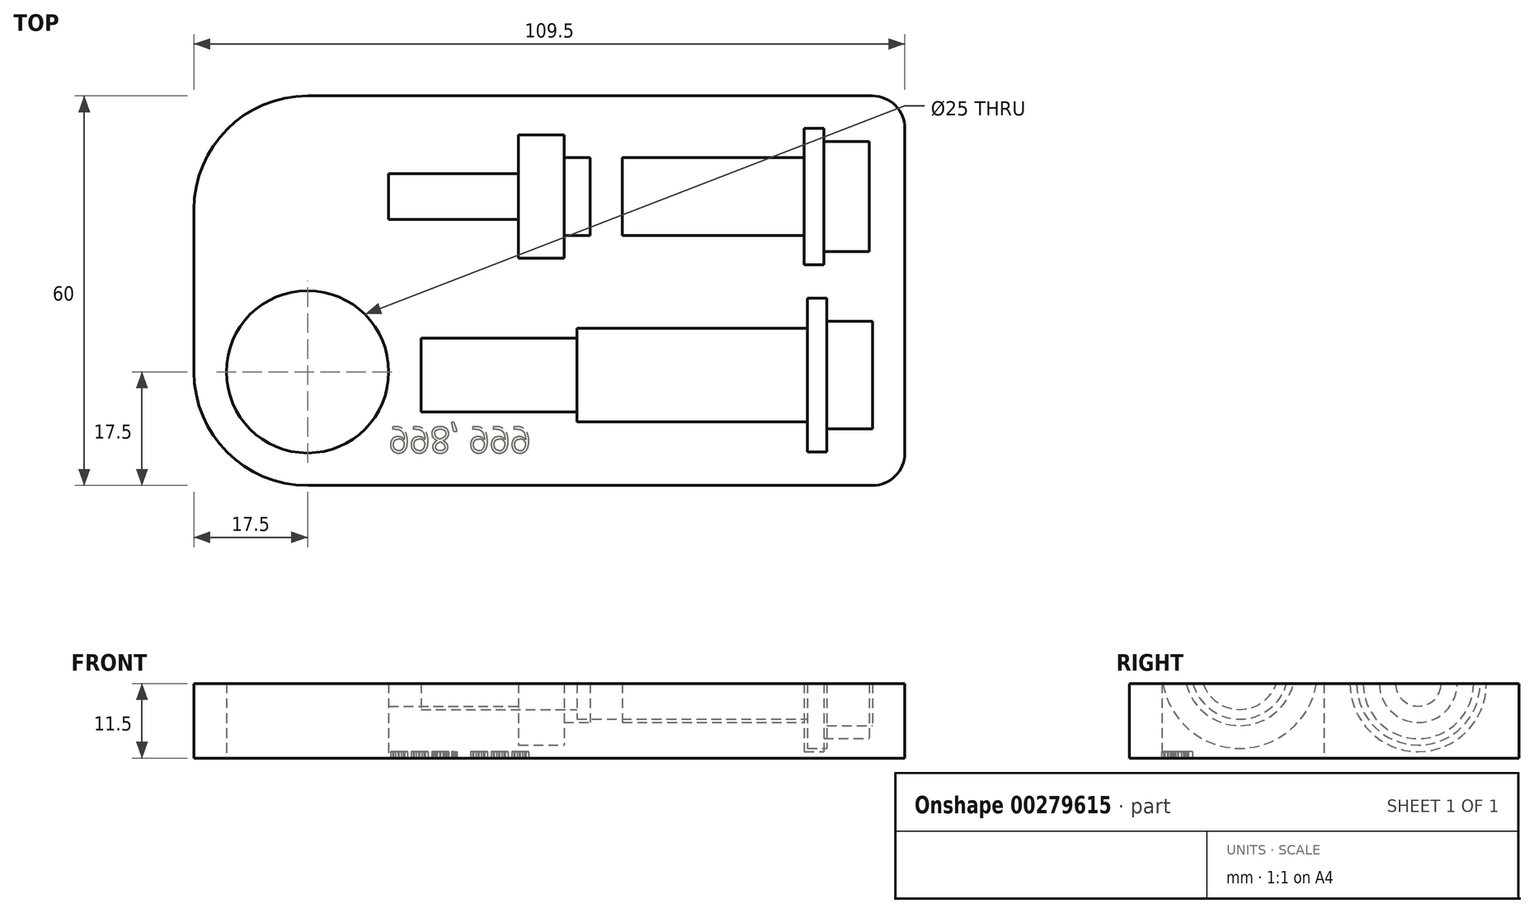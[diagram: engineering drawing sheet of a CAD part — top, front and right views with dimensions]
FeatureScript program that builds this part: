
annotation { "Feature Type Name" : "Feature", "Feature Type Description" : "" }
export const myFeature = defineFeature(function(context is Context, id is Id, definition is map)
    precondition{}
    {
        {
            var Q0;
            Q0=qCreatedBy(makeId("Top.planeOp"),FACE);
            var sketch = newSketch(context, id + "F0", { "sketchPlane" : qUnion([Q0])});
            skLineSegment(sketch, "E0.bottom", {"start": v(17.5, 0) * mm, "end": v(104.5, 0) * mm});
            skLineSegment(sketch, "E0.top", {"start": v(17.5, 60) * mm, "end": v(104.5, 60) * mm});
            skLineSegment(sketch, "E0.left", {"start": v(0, 17.5) * mm, "end": v(0, 42.5) * mm});
            skLineSegment(sketch, "E0.right", {"start": v(109.5, 5) * mm, "end": v(109.5, 55) * mm});
            skLineSegment(sketch, "E1.bottom", {"start": v(0, 0) * mm, "end": v(17.5, 0) * mm, "construction": true});
            skLineSegment(sketch, "E1.top", {"start": v(0, 17.5) * mm, "end": v(17.5, 17.5) * mm, "construction": true});
            skLineSegment(sketch, "E1.left", {"start": v(0, 0) * mm, "end": v(0, 17.5) * mm, "construction": true});
            skLineSegment(sketch, "E1.right", {"start": v(17.5, 0) * mm, "end": v(17.5, 17.5) * mm, "construction": true});
            skCircle(sketch, "E2", {"center": v(17.5, 17.5) * mm, "radius": 12.5 * mm});
            skPoint(sketch, "E3.visualSharp", {"position": v(0, 0) * mm});
            skArc(sketch, "E3.filletArc", {"start": v(0, 17.5) * mm, "mid": v(5.13, 5.13) * mm, "end": v(17.5, 0) * mm});
            skPoint(sketch, "E4.visualSharp", {"position": v(0, 60) * mm});
            skArc(sketch, "E4.filletArc", {"start": v(17.5, 60) * mm, "mid": v(5.13, 54.87) * mm, "end": v(0, 42.5) * mm});
            skPoint(sketch, "E5.visualSharp", {"position": v(109.5, 60) * mm});
            skArc(sketch, "E5.filletArc", {"start": v(109.5, 55) * mm, "mid": v(108.04, 58.54) * mm, "end": v(104.5, 60) * mm});
            skPoint(sketch, "E6.visualSharp", {"position": v(109.5, 0) * mm});
            skArc(sketch, "E6.filletArc", {"start": v(104.5, 0) * mm, "mid": v(108.04, 1.46) * mm, "end": v(109.5, 5) * mm});
            skSolve(sketch);
        }
        {
            var Q0;
            Q0=makeQuery(id+"F0.imprint","IMPRINT",FACE,{"disambiguationData":[TD([[makeQuery(id+"F0.imprint","IMPRINT",EDGE,{"derivedFrom":sQuery(id+"F0.wireOp",EDGE,"E0.bottom")}),1.0]])]});
            extrude(context, id + "F1", {"entities" : qUnion([Q0]), "depth" : 11.5 * mm});
        }
        {
            var Q0;
            Q0=makeQuery(id+"F1.opExtrude","CAP_FACE",FACE,{"disambiguationData":[OSD([sQuery(id+"F0.wireOp",EDGE,"E0.bottom"),sQuery(id+"F0.wireOp",EDGE,"E0.top"),sQuery(id+"F0.wireOp",EDGE,"E0.right"),sQuery(id+"F0.wireOp",EDGE,"E2"),sQuery(id+"F0.wireOp",EDGE,"E3.filletArc"),sQuery(id+"F0.wireOp",EDGE,"E4.filletArc"),sQuery(id+"F0.wireOp",EDGE,"E5.filletArc"),sQuery(id+"F0.wireOp",EDGE,"E6.filletArc")])],"isStart":false});
            var sketch = newSketch(context, id + "F2", { "sketchPlane" : qUnion([Q0])});
            skLineSegment(sketch, "E7.bottom", {"start": v(0, 0) * mm, "end": v(35, 0) * mm, "construction": true});
            skLineSegment(sketch, "E7.top", {"start": v(0, 17) * mm, "end": v(35, 17) * mm, "construction": true});
            skLineSegment(sketch, "E7.left", {"start": v(0, 0) * mm, "end": v(0, 17) * mm, "construction": true});
            skLineSegment(sketch, "E7.right", {"start": v(35, 0) * mm, "end": v(35, 11) * mm, "construction": true});
            skLineSegment(sketch, "E8", {"start": v(35, 17) * mm, "end": v(35, 44.5) * mm, "construction": true});
            skLineSegment(sketch, "E9.bottom", {"start": v(30, 44.5) * mm, "end": v(50, 44.5) * mm});
            skLineSegment(sketch, "E10.bottom", {"start": v(50, 44.5) * mm, "end": v(57, 44.5) * mm});
            skLineSegment(sketch, "E10.top", {"start": v(50, 35) * mm, "end": v(57, 35) * mm});
            skLineSegment(sketch, "E10.left", {"start": v(50, 41) * mm, "end": v(50, 35) * mm});
            skLineSegment(sketch, "E10.right", {"start": v(57, 38.5) * mm, "end": v(57, 35) * mm});
            skLineSegment(sketch, "E11.bottom", {"start": v(57, 44.5) * mm, "end": v(61, 44.5) * mm});
            skLineSegment(sketch, "E11.top", {"start": v(57, 38.5) * mm, "end": v(61, 38.5) * mm});
            skLineSegment(sketch, "E11.right", {"start": v(61, 44.5) * mm, "end": v(61, 38.5) * mm});
            skLineSegment(sketch, "E12", {"start": v(61, 44.5) * mm, "end": v(66, 44.5) * mm, "construction": true});
            skLineSegment(sketch, "E13.bottom", {"start": v(66, 44.5) * mm, "end": v(94, 44.5) * mm});
            skLineSegment(sketch, "E13.top", {"start": v(66, 38.5) * mm, "end": v(94, 38.5) * mm});
            skLineSegment(sketch, "E13.left", {"start": v(66, 44.5) * mm, "end": v(66, 38.5) * mm});
            skLineSegment(sketch, "E14.bottom", {"start": v(94, 44.5) * mm, "end": v(97, 44.5) * mm});
            skLineSegment(sketch, "E14.top", {"start": v(94, 34) * mm, "end": v(97, 34) * mm});
            skLineSegment(sketch, "E14.left", {"start": v(94, 38.5) * mm, "end": v(94, 34) * mm});
            skLineSegment(sketch, "E14.right", {"start": v(97, 36) * mm, "end": v(97, 34) * mm});
            skLineSegment(sketch, "E15.bottom", {"start": v(97, 44.5) * mm, "end": v(104, 44.5) * mm});
            skLineSegment(sketch, "E15.top", {"start": v(97, 36) * mm, "end": v(104, 36) * mm});
            skLineSegment(sketch, "E15.right", {"start": v(104, 44.5) * mm, "end": v(104, 36) * mm});
            skLineSegment(sketch, "E16", {"start": v(35, 44.5) * mm, "end": v(30, 44.5) * mm, "construction": true});
            skLineSegment(sketch, "E17", {"start": v(50, 41) * mm, "end": v(30, 41) * mm});
            skLineSegment(sketch, "E18", {"start": v(30, 41) * mm, "end": v(30, 44.5) * mm});
            skSolve(sketch);
        }
        {
            var Q0;
            Q0=makeQuery(id+"F2.imprint","IMPRINT",FACE,{"disambiguationData":[TD([[makeQuery(id+"F2.imprint","IMPRINT",EDGE,{"derivedFrom":sQuery(id+"F2.wireOp",EDGE,"E9.bottom")}),-1.0]])]});
            var Q1;
            Q1=makeQuery(id+"F2.imprint","IMPRINT",FACE,{"disambiguationData":[TD([[makeQuery(id+"F2.imprint","IMPRINT",EDGE,{"derivedFrom":sQuery(id+"F2.wireOp",EDGE,"E13.bottom")}),-1.0]])]});
            var Q2;
            Q2=sQuery(id+"F2.wireOp",EDGE,"E13.bottom");
            revolve(context, id + "F3", {"operationType" : NewBodyOperationType.REMOVE, "entities" : qUnion([Q0, Q1]), "axis" : qUnion([Q2]), "revolveType" : RevolveType.FULL, "oppositeDirection" : true});
        }
        {
            var Q0;
            Q0=makeQuery(id+"F1.opExtrude","CAP_FACE",FACE,{"disambiguationData":[OSD([sQuery(id+"F0.wireOp",EDGE,"E0.bottom"),sQuery(id+"F0.wireOp",EDGE,"E0.top"),sQuery(id+"F0.wireOp",EDGE,"E0.left"),sQuery(id+"F0.wireOp",EDGE,"E0.right"),sQuery(id+"F0.wireOp",EDGE,"E2"),sQuery(id+"F0.wireOp",EDGE,"E3.filletArc"),sQuery(id+"F0.wireOp",EDGE,"E4.filletArc"),sQuery(id+"F0.wireOp",EDGE,"E5.filletArc"),sQuery(id+"F0.wireOp",EDGE,"E6.filletArc")])],"isStart":false});
            cPlane(context, id + "F4", {"entities" : qUnion([Q0]), "cplaneType" : CPlaneType.OFFSET, "offset" : 2 * mm, "width" : 150 * mm, "height" : 150 * mm});
        }
        {
            var Q0;
            Q0=qCreatedBy(id+"F4.planeOp",FACE);
            var sketch = newSketch(context, id + "F5", { "sketchPlane" : qUnion([Q0])});
            skLineSegment(sketch, "E19.bottom", {"start": v(59, 17) * mm, "end": v(94.5, 17) * mm});
            skLineSegment(sketch, "E19.top", {"start": v(59, 9.5) * mm, "end": v(94.5, 9.5) * mm});
            skLineSegment(sketch, "E19.left", {"start": v(59, 11) * mm, "end": v(59, 9.5) * mm});
            skLineSegment(sketch, "E20.bottom", {"start": v(94.5, 17) * mm, "end": v(97.5, 17) * mm});
            skLineSegment(sketch, "E20.top", {"start": v(94.5, 5) * mm, "end": v(97.5, 5) * mm});
            skLineSegment(sketch, "E20.left", {"start": v(94.5, 9.5) * mm, "end": v(94.5, 5) * mm});
            skLineSegment(sketch, "E20.right", {"start": v(97.5, 8.5) * mm, "end": v(97.5, 5) * mm});
            skLineSegment(sketch, "E21.bottom", {"start": v(97.5, 17) * mm, "end": v(104.5, 17) * mm});
            skLineSegment(sketch, "E21.top", {"start": v(97.5, 8.5) * mm, "end": v(104.5, 8.5) * mm});
            skLineSegment(sketch, "E21.right", {"start": v(104.5, 17) * mm, "end": v(104.5, 8.5) * mm});
            skLineSegment(sketch, "E22", {"start": v(35, 17) * mm, "end": v(35, 11) * mm});
            skLineSegment(sketch, "E23.trimOffspring", {"start": v(35, 17) * mm, "end": v(59, 17) * mm});
            skLineSegment(sketch, "E24.trimOffspring", {"start": v(35, 11) * mm, "end": v(59, 11) * mm});
            skLineSegment(sketch, "E25.bottom", {"start": v(0, 0) * mm, "end": v(35, 0) * mm, "construction": true});
            skLineSegment(sketch, "E25.top", {"start": v(0, 17) * mm, "end": v(35, 17) * mm, "construction": true});
            skLineSegment(sketch, "E25.left", {"start": v(0, 0) * mm, "end": v(0, 17) * mm, "construction": true});
            skLineSegment(sketch, "E25.right", {"start": v(35, 0) * mm, "end": v(35, 17) * mm, "construction": true});
            skSolve(sketch);
        }
        {
            var Q0;
            Q0=makeQuery(id+"F5.imprint","IMPRINT",FACE,{"disambiguationData":[TD([[makeQuery(id+"F5.imprint","IMPRINT",EDGE,{"derivedFrom":sQuery(id+"F5.wireOp",EDGE,"E19.bottom")}),-1.0]])]});
            var Q1;
            Q1=sQuery(id+"F5.wireOp",EDGE,"E23.trimOffspring");
            revolve(context, id + "F6", {"operationType" : NewBodyOperationType.REMOVE, "entities" : qUnion([Q0]), "axis" : qUnion([Q1]), "revolveType" : RevolveType.FULL, "oppositeDirection" : true});
        }
        {
            var Q0;
            Q0=makeQuery(id+"F1.opExtrude","CAP_FACE",FACE,{"disambiguationData":[OSD([sQuery(id+"F0.wireOp",EDGE,"E0.bottom"),sQuery(id+"F0.wireOp",EDGE,"E0.top"),sQuery(id+"F0.wireOp",EDGE,"E0.left"),sQuery(id+"F0.wireOp",EDGE,"E0.right"),sQuery(id+"F0.wireOp",EDGE,"E2"),sQuery(id+"F0.wireOp",EDGE,"E3.filletArc"),sQuery(id+"F0.wireOp",EDGE,"E4.filletArc"),sQuery(id+"F0.wireOp",EDGE,"E5.filletArc"),sQuery(id+"F0.wireOp",EDGE,"E6.filletArc")])],"isStart":true});
            var sketch = newSketch(context, id + "F7", { "sketchPlane" : qUnion([Q0])});
            skLineSegment(sketch, "E26.bottom", {"start": v(0, 0) * mm, "end": v(30, 0) * mm, "construction": true});
            skLineSegment(sketch, "E26.top", {"start": v(0, -5) * mm, "end": v(30, -5) * mm, "construction": true});
            skLineSegment(sketch, "E26.left", {"start": v(0, 0) * mm, "end": v(0, -5) * mm, "construction": true});
            skLineSegment(sketch, "E26.right", {"start": v(30, 0) * mm, "end": v(30, -5) * mm, "construction": true});
            skText(sketch, "E27", { "text": "998, 999", "fontName": "OpenSans-Regular.ttf"});
            const initialGuessF7  = {"E27": [0.03, -0.009, 1, 0, 0.004]};
            skSetInitialGuess(sketch, initialGuessF7);
            skSolve(sketch);
        }
        {
            var Q0;
            Q0 = qSketchRegion(id + "F7", true);
            extrude(context, id + "F8", {"entities" : qUnion([Q0]), "operationType" : NewBodyOperationType.REMOVE, "oppositeDirection" : true, "depth" : 1 * mm});
        }
    });
